# Revit family: Urinal-Wiloughby-1560-WWU
name_source: partatom
category: Plumbing Fixtures
revit_build: Autodesk Revit 2015 (Build: 20140606_1530(x64)
units: mm (PartAtom-declared; Revit-internal decimal feet)

## types (5) — shared parameters
CW Connection = No
Default Elevation = 0' - 0"
Fixture Body = Stainless Steel AISI 304-Willoughby
HW Connection = No
Manufacturer = Willoughby Industries
Revision = A
Vent Connection = No
Waste Connection = Yes
Waste DIA = 2"

## per-type parameters (varying)
| type | 60" | Description | Model | URL | Width |
| 1536 | No | 36" Trough Urinal | WWU-1536 | www.willoughby-ind.com | 3' - 0" |
| 1548 | No | 36" Trough Urinal | WWU-1536 | www.willoughby-ind.com | 4' - 0" |
| 1560 | Yes | 60" Trough Urinal | WWU-1560 | https://www.willoughby-ind.com | 5' - 0" |
| 1572 | No | 36" Trough Urinal | WWU-1536 | www.willoughby-ind.com | 6' - 0" |
| 1596 | No | 36" Trough Urinal | WWU-1536 | www.willoughby-ind.com | 8' - 0" |

## geometry (parser evidence)
native form markers: Sweep x2
no freeform markers — native parametric forms only
